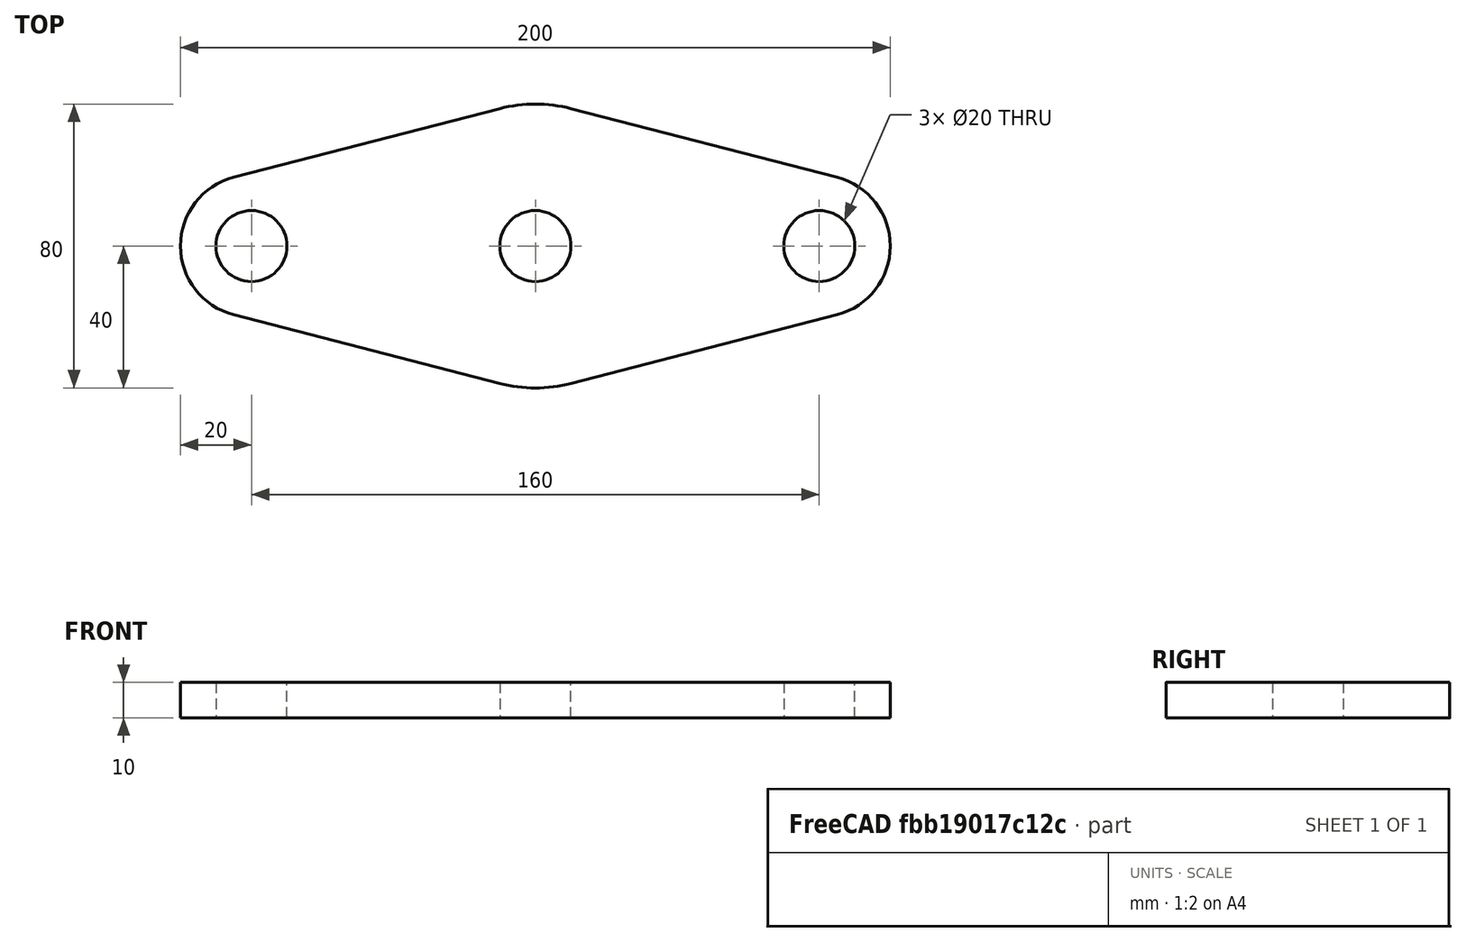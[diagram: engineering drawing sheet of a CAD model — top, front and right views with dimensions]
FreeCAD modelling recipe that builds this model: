
FCSTD DOCUMENT  (FreeCAD 0.20R29177 +426 (Git))
Label: rotary-1
License: All rights reserved
LicenseURL: http://en.wikipedia.org/wiki/All_rights_reserved
objects: Sketcher::SketchObject×1, PartDesign::Body×1, Part::Extrusion×1
note: 3 computed .brp shape members not serialized (recipe doc carries the construction recipe); baked Part::Feature solids carry a one-line shape summary decoded from their .brp

FEATURE [Sketcher::SketchObject] Sketch
  FullyConstrained = false
  MapMode = 5
  Support = -> [XY_Plane]
  sketch-geometry (14):
    g0: Circle CenterX=0 CenterY=0 CenterZ=0 NormalX=0 NormalY=0 NormalZ=1 AngleXU=0 Radius=100
    g1: ArcOfCircle CenterX=0 CenterY=0 CenterZ=0 NormalX=0 NormalY=0 NormalZ=1 AngleXU=0 Radius=40 StartAngle=4.45971 EndAngle=4.96507
    g2: LineSegment StartX=-80 StartY=0 StartZ=0 EndX=0 EndY=0 EndZ=0
    g3: LineSegment StartX=0 StartY=0 StartZ=0 EndX=80 EndY=0 EndZ=0
    g4: ArcOfCircle CenterX=-80 CenterY=0 CenterZ=0 NormalX=0 NormalY=0 NormalZ=1 AngleXU=0 Radius=20 StartAngle=1.82348 EndAngle=4.45971
    g5: ArcOfCircle CenterX=80 CenterY=0 CenterZ=0 NormalX=0 NormalY=0 NormalZ=1 AngleXU=0 Radius=20 StartAngle=4.96507 EndAngle=7.6013
    g6: LineSegment StartX=-85 StartY=19.3649 StartZ=0 EndX=-10 EndY=38.7298 EndZ=0
    g7: LineSegment StartX=10 StartY=38.7298 StartZ=0 EndX=85 EndY=19.3649 EndZ=0
    g8: LineSegment StartX=85 StartY=-19.3649 StartZ=0 EndX=10 EndY=-38.7298 EndZ=0
    g9: LineSegment StartX=-10 StartY=-38.7298 StartZ=0 EndX=-85 EndY=-19.3649 EndZ=0
    g10: Circle CenterX=0 CenterY=0 CenterZ=0 NormalX=0 NormalY=0 NormalZ=1 AngleXU=0 Radius=10
    g11: ArcOfCircle CenterX=0 CenterY=0 CenterZ=0 NormalX=0 NormalY=0 NormalZ=1 AngleXU=0 Radius=40 StartAngle=1.31812 EndAngle=1.82348
    g12: Circle CenterX=-80 CenterY=0 CenterZ=0 NormalX=0 NormalY=0 NormalZ=1 AngleXU=0 Radius=10
    g13: Circle CenterX=80 CenterY=0 CenterZ=0 NormalX=0 NormalY=0 NormalZ=1 AngleXU=0 Radius=10
  constraints (30):
    c: Coincident(g0,g-1)
    c: Diameter(g0) = 200
    c: Coincident(g1,g0)
    c: Diameter(g1) = 80
    c: PointOnObject(g2,g-1)
    c: Coincident(g2,g0)
    c: Coincident(g3,g0)
    c: PointOnObject(g3,g-1)
    c: Equal(g2,g3)
    c: DistanceX(g2,g3) = 160
    c: Coincident(g4,g2)
    c: Tangent(g4,g0)
    c: Coincident(g5,g3)
    c: Tangent(g5,g0)
    c: Tangent(g4,g6) = 1.5708
    c: Tangent(g4,g9) = 1.5708
    c: Tangent(g5,g8) = 1.5708
    c: Tangent(g5,g7) = 1.5708
    c: Coincident(g10,g0)
    c: Equal(g1,g11)
    c: Coincident(g11,g7)
    c: Coincident(g1,g11)
    c: Tangent(g1,g9) = 1.5708
    c: Tangent(g1,g8) = 1.5708
    c: Coincident(g12,g2)
    c: Equal(g12,g10)
    c: Diameter(g12) = 20
    c: Coincident(g13,g3)
    c: Equal(g13,g10)
    c: Tangent(g6,g11) = 1.5708
FEATURE [PartDesign::Body] Body
  Group = -> [Sketch]
  Origin = -> Origin
FEATURE [Part::Extrusion] Extrude
  Base = -> Sketch
  Dir = (0,0,1)
  DirMode = 2
  FaceMakerClass = Part::FaceMakerBullseye
  LengthFwd = 10
  LengthRev = 0
  Solid = true
  Symmetric = false
